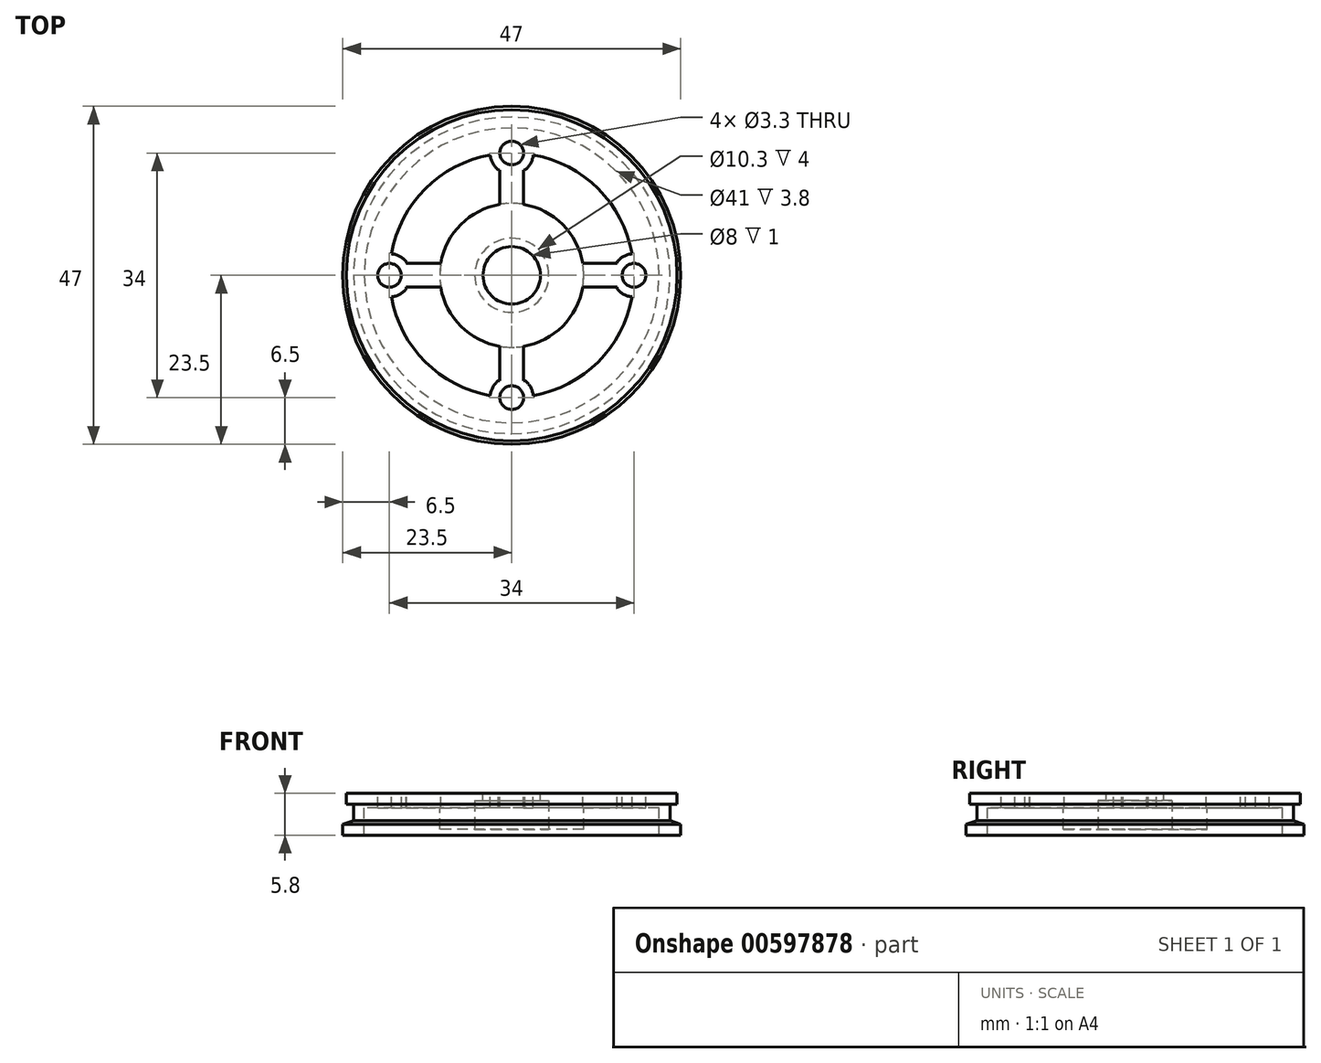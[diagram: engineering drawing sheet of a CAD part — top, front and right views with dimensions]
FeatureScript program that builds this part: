
annotation { "Feature Type Name" : "Feature", "Feature Type Description" : "" }
export const myFeature = defineFeature(function(context is Context, id is Id, definition is map)
    precondition{}
    {
        {
            var Q0;
            Q0=qCreatedBy(makeId("Front.planeOp"),FACE);
            var sketch = newSketch(context, id + "F0", { "sketchPlane" : qUnion([Q0])});
            skLineSegment(sketch, "E0", {"start": v(0, 18.35) * mm, "end": v(0, 16.35) * mm});
            skLineSegment(sketch, "E1", {"start": v(20.5, 12.55) * mm, "end": v(23, 12.55) * mm});
            skLineSegment(sketch, "E2", {"start": v(22, 16.85) * mm, "end": v(23, 16.85) * mm});
            skLineSegment(sketch, "E3", {"start": v(23, 16.85) * mm, "end": v(23, 18.35) * mm});
            skLineSegment(sketch, "E4", {"start": v(23, 18.35) * mm, "end": v(14.75, 18.35) * mm});
            skLineSegment(sketch, "E5", {"start": v(20.5, 12.55) * mm, "end": v(20.5, 16.35) * mm});
            skLineSegment(sketch, "E6", {"start": v(20.5, 16.35) * mm, "end": v(14.75, 16.35) * mm});
            skLineSegment(sketch, "E7", {"start": v(14.75, 18.35) * mm, "end": v(14.75, 16.35) * mm});
            skLineSegment(sketch, "E8", {"start": v(22, 16.85) * mm, "end": v(22, 14.58) * mm});
            skLineSegment(sketch, "E9.bottom", {"start": v(23, 14.05) * mm, "end": v(23.5, 14.05) * mm});
            skLineSegment(sketch, "E9.top", {"start": v(23, 12.55) * mm, "end": v(23.5, 12.55) * mm});
            skLineSegment(sketch, "E9.right", {"start": v(23.5, 14.05) * mm, "end": v(23.5, 12.55) * mm});
            skLineSegment(sketch, "E10", {"start": v(23.5, 14.05) * mm, "end": v(22, 14.58) * mm});
            skSolve(sketch);
        }
        {
            var Q0;
            Q0=makeQuery(id+"F0.imprint","IMPRINT",FACE,{"disambiguationData":[TD([[makeQuery(id+"F0.imprint","IMPRINT",EDGE,{"derivedFrom":sQuery(id+"F0.wireOp",EDGE,"E1")}),1.0]])]});
            var Q1;
            Q1=sQuery(id+"F0.wireOp",EDGE,"E0");
            revolve(context, id + "F1", {"entities" : qUnion([Q0]), "axis" : qUnion([Q1]), "revolveType" : RevolveType.FULL});
        }
        {
            var Q0;
            Q0=makeQuery(id+"F1.opRevolve","SWEPT_FACE",FACE,{"disambiguationData":[OSD([sQuery(id+"F0.wireOp",EDGE,"E4")])]});
            var sketch = newSketch(context, id + "F2", { "sketchPlane" : qUnion([Q0])});
            skCircle(sketch, "E11", {"center": v(0, 17) * mm, "radius": 1.65 * mm});
            skCircle(sketch, "E12", {"center": v(0, -17) * mm, "radius": 1.65 * mm});
            skCircle(sketch, "E13", {"center": v(17, 0) * mm, "radius": 1.65 * mm});
            skCircle(sketch, "E14", {"center": v(-17, 0) * mm, "radius": 1.65 * mm});
            skSolve(sketch);
        }
        {
            var Q0;
            Q0=makeQuery(id+"F2.imprint","IMPRINT",FACE,{"disambiguationData":[TD([[makeQuery(id+"F2.imprint","IMPRINT",EDGE,{"derivedFrom":sQuery(id+"F2.wireOp",EDGE,"E11")}),1.0]])]});
            var Q1;
            Q1=makeQuery(id+"F2.imprint","IMPRINT",FACE,{"disambiguationData":[TD([[makeQuery(id+"F2.imprint","IMPRINT",EDGE,{"derivedFrom":sQuery(id+"F2.wireOp",EDGE,"E13")}),1.0]])]});
            var Q2;
            Q2=makeQuery(id+"F2.imprint","IMPRINT",FACE,{"disambiguationData":[TD([[makeQuery(id+"F2.imprint","IMPRINT",EDGE,{"derivedFrom":sQuery(id+"F2.wireOp",EDGE,"E14")}),1.0]])]});
            var Q3;
            Q3=makeQuery(id+"F2.imprint","IMPRINT",FACE,{"disambiguationData":[TD([[makeQuery(id+"F2.imprint","IMPRINT",EDGE,{"derivedFrom":sQuery(id+"F2.wireOp",EDGE,"E12")}),1.0]])]});
            extrude(context, id + "F3", {"entities" : qUnion([Q0, Q1, Q2, Q3]), "operationType" : NewBodyOperationType.REMOVE, "endBound" : BoundingType.THROUGH_ALL, "oppositeDirection" : true, "depth" : 25 * mm, "offsetDistance" : 25 * mm});
        }
        {
            var Q0;
            Q0=makeQuery(id+"F1.opRevolve","SWEPT_FACE",FACE,{"disambiguationData":[OSD([sQuery(id+"F0.wireOp",EDGE,"E4")])]});
            var sketch = newSketch(context, id + "F4", { "sketchPlane" : qUnion([Q0])});
            skArc(sketch, "E15", {"start": v(-1.65, 9.86) * mm, "mid": v(-7.07, 7.07) * mm, "end": v(-9.86, 1.65) * mm});
            skLineSegment(sketch, "E16", {"start": v(-17.07, 1.65) * mm, "end": v(-9.86, 1.65) * mm});
            skLineSegment(sketch, "E17", {"start": v(17, -1.65) * mm, "end": v(9.86, -1.65) * mm});
            skLineSegment(sketch, "E18", {"start": v(1.65, 16.99) * mm, "end": v(1.65, 9.86) * mm});
            skLineSegment(sketch, "E19", {"start": v(-1.65, -17) * mm, "end": v(-1.65, -9.86) * mm});
            skLineSegment(sketch, "E20.trimOffspring", {"start": v(9.86, 1.65) * mm, "end": v(17, 1.65) * mm});
            skLineSegment(sketch, "E21.trimOffspring", {"start": v(-1.65, 9.86) * mm, "end": v(-1.65, 16.99) * mm});
            skLineSegment(sketch, "E22.trimOffspring", {"start": v(1.65, -9.86) * mm, "end": v(1.65, -17) * mm});
            skArc(sketch, "E23.trimOffspring", {"start": v(9.86, 1.65) * mm, "mid": v(7.07, 7.07) * mm, "end": v(1.65, 9.86) * mm});
            skLineSegment(sketch, "E24.trimOffspring", {"start": v(-9.86, -1.65) * mm, "end": v(-17, -1.65) * mm});
            skArc(sketch, "E25.trimOffspring", {"start": v(1.65, -9.86) * mm, "mid": v(7.07, -7.07) * mm, "end": v(9.86, -1.65) * mm});
            skArc(sketch, "E26.trimOffspring", {"start": v(-9.86, -1.65) * mm, "mid": v(-7.07, -7.07) * mm, "end": v(-1.65, -9.86) * mm});
            skSolve(sketch);
        }
        {
            var Q0;
            {var subQ5=sQuery(id+"F4.wireOp",EDGE,"E15");Q0=makeQuery(id+"F4.imprint","IMPRINT",FACE,{"disambiguationData":[TD([[makeQuery(id+"F4.imprint","IMPRINT",EDGE,{"derivedFrom":subQ5}),1.0]])]});}
            var Q1;
            {var subQ0=sQuery(id+"F4.wireOp",EDGE,"E18");var subQ1=makeQuery(id+"F3.boolean.opBoolean","COPY",EDGE,{"derivedFrom":makeQuery(id+"F3.opExtrude","CAP_EDGE",EDGE,{"disambiguationData":[OSD([sQuery(id+"F2.wireOp",EDGE,"E11")])],"isStart":true})});var subQ2=makeQuery(id+"F4.imprint","INTERSECT",VERTEX,{"derivedFrom":[subQ1,subQ0]});Q1=makeQuery(id+"F4.imprint","IMPRINT",FACE,{"disambiguationData":[TD([[makeQuery(id+"F4.imprint","IMPRINT",EDGE,{"disambiguationData":[TD([[subQ2,1.0]])],"derivedFrom":subQ1}),-1.0]])]});}
            var Q2;
            {var subQ0=sQuery(id+"F4.wireOp",EDGE,"E17");var subQ1=makeQuery(id+"F3.boolean.opBoolean","COPY",EDGE,{"derivedFrom":makeQuery(id+"F3.opExtrude","CAP_EDGE",EDGE,{"disambiguationData":[OSD([sQuery(id+"F2.wireOp",EDGE,"E13")])],"isStart":true})});var subQ2=makeQuery(id+"F4.imprint","INTERSECT",VERTEX,{"derivedFrom":[subQ1,subQ0]});Q2=makeQuery(id+"F4.imprint","IMPRINT",FACE,{"disambiguationData":[TD([[makeQuery(id+"F4.imprint","IMPRINT",EDGE,{"disambiguationData":[TD([[subQ2,1.0]])],"derivedFrom":subQ1}),-1.0]])]});}
            var Q3;
            {var subQ1=makeQuery(id+"F3.boolean.opBoolean","COPY",EDGE,{"derivedFrom":makeQuery(id+"F3.opExtrude","CAP_EDGE",EDGE,{"disambiguationData":[OSD([sQuery(id+"F2.wireOp",EDGE,"E14")])],"isStart":true})});var subQ5=sQuery(id+"F4.wireOp",EDGE,"E24.trimOffspring");var subQ6=makeQuery(id+"F4.imprint","INTERSECT",VERTEX,{"derivedFrom":[subQ1,subQ5]});Q3=makeQuery(id+"F4.imprint","IMPRINT",FACE,{"disambiguationData":[TD([[makeQuery(id+"F4.imprint","IMPRINT",EDGE,{"disambiguationData":[TD([[subQ6,-1.0]])],"derivedFrom":subQ1}),-1.0]])]});}
            var Q4;
            {var subQ0=sQuery(id+"F4.wireOp",EDGE,"E19");var subQ1=makeQuery(id+"F3.boolean.opBoolean","COPY",EDGE,{"derivedFrom":makeQuery(id+"F3.opExtrude","CAP_EDGE",EDGE,{"disambiguationData":[OSD([sQuery(id+"F2.wireOp",EDGE,"E12")])],"isStart":true})});var subQ2=makeQuery(id+"F4.imprint","INTERSECT",VERTEX,{"derivedFrom":[subQ1,subQ0]});Q4=makeQuery(id+"F4.imprint","IMPRINT",FACE,{"disambiguationData":[TD([[makeQuery(id+"F4.imprint","IMPRINT",EDGE,{"disambiguationData":[TD([[subQ2,1.0]])],"derivedFrom":subQ1}),-1.0]])]});}
            extrude(context, id + "F5", {"entities" : qUnion([Q0, Q1, Q2, Q3, Q4]), "operationType" : NewBodyOperationType.ADD, "oppositeDirection" : true, "depth" : 2 * mm, "offsetDistance" : 25 * mm});
        }
        {
            var Q0;
            Q0=makeQuery(id+"F5.boolean.opBoolean","MERGE",FACE,{"derivedFrom":[makeQuery(id+"F1.opRevolve","SWEPT_FACE",FACE,{"disambiguationData":[OSD([sQuery(id+"F0.wireOp",EDGE,"E4")])]}),makeQuery(id+"F5.opExtrude","CAP_FACE",FACE,{"disambiguationData":[OSD([sQuery(id+"F2.wireOp",EDGE,"E11"),sQuery(id+"F2.wireOp",EDGE,"E12"),sQuery(id+"F2.wireOp",EDGE,"E13"),sQuery(id+"F2.wireOp",EDGE,"E14"),sQuery(id+"F4.wireOp",EDGE,"E15"),sQuery(id+"F4.wireOp",EDGE,"E16"),sQuery(id+"F4.wireOp",EDGE,"E17"),sQuery(id+"F4.wireOp",EDGE,"E18"),sQuery(id+"F4.wireOp",EDGE,"E19"),sQuery(id+"F4.wireOp",EDGE,"E20.trimOffspring"),sQuery(id+"F4.wireOp",EDGE,"E21.trimOffspring"),sQuery(id+"F4.wireOp",EDGE,"E22.trimOffspring"),sQuery(id+"F4.wireOp",EDGE,"E23.trimOffspring"),sQuery(id+"F4.wireOp",EDGE,"E24.trimOffspring"),sQuery(id+"F4.wireOp",EDGE,"E25.trimOffspring"),sQuery(id+"F4.wireOp",EDGE,"E26.trimOffspring")])],"isStart":true})]});
            var sketch = newSketch(context, id + "F6", { "sketchPlane" : qUnion([Q0])});
            skArc(sketch, "E27", {"start": v(-2.99, 16.74) * mm, "mid": v(-12.02, 12.02) * mm, "end": v(-16.74, 2.99) * mm});
            skArc(sketch, "E28", {"start": v(-2.99, 16.74) * mm, "mid": v(0, 14) * mm, "end": v(2.99, 16.74) * mm});
            skArc(sketch, "E29", {"start": v(16.74, 2.99) * mm, "mid": v(14, 0) * mm, "end": v(16.74, -2.99) * mm});
            skArc(sketch, "E30", {"start": v(-16.74, -2.99) * mm, "mid": v(-14, 0) * mm, "end": v(-16.74, 2.99) * mm});
            skArc(sketch, "E31", {"start": v(2.99, -16.74) * mm, "mid": v(0, -14) * mm, "end": v(-2.99, -16.74) * mm});
            skPoint(sketch, "E32.0.midPoint", {"position": v(3.11, -5.36) * mm});
            skArc(sketch, "E33.trimOffspring", {"start": v(-16.74, -2.99) * mm, "mid": v(-12.02, -12.02) * mm, "end": v(-2.99, -16.74) * mm});
            skArc(sketch, "E34.trimOffspring", {"start": v(2.99, -16.74) * mm, "mid": v(12.02, -12.02) * mm, "end": v(16.74, -2.99) * mm});
            skArc(sketch, "E35.trimOffspring", {"start": v(16.74, 2.99) * mm, "mid": v(12.02, 12.02) * mm, "end": v(2.99, 16.74) * mm});
            skPoint(sketch, "E36.orphan", {"position": v(-0.02, 7.16) * mm});
            skPoint(sketch, "E37.orphan", {"position": v(0.02, -7.16) * mm});
            skPoint(sketch, "E38.orphan", {"position": v(6.2, -3.56) * mm});
            skSolve(sketch);
        }
        {
            var Q0;
            {var subQ0=sQuery(id+"F6.wireOp",EDGE,"E27");Q0=makeQuery(id+"F6.imprint","IMPRINT",FACE,{"disambiguationData":[TD([[makeQuery(id+"F6.imprint","IMPRINT",EDGE,{"derivedFrom":subQ0}),1.0]])]});}
            var Q1;
            {var subQ0=sQuery(id+"F6.wireOp",EDGE,"E35.trimOffspring");Q1=makeQuery(id+"F6.imprint","IMPRINT",FACE,{"disambiguationData":[TD([[makeQuery(id+"F6.imprint","IMPRINT",EDGE,{"derivedFrom":subQ0}),1.0]])]});}
            var Q2;
            {var subQ0=sQuery(id+"F6.wireOp",EDGE,"E34.trimOffspring");Q2=makeQuery(id+"F6.imprint","IMPRINT",FACE,{"disambiguationData":[TD([[makeQuery(id+"F6.imprint","IMPRINT",EDGE,{"derivedFrom":subQ0}),1.0]])]});}
            var Q3;
            {var subQ0=sQuery(id+"F6.wireOp",EDGE,"E33.trimOffspring");Q3=makeQuery(id+"F6.imprint","IMPRINT",FACE,{"disambiguationData":[TD([[makeQuery(id+"F6.imprint","IMPRINT",EDGE,{"derivedFrom":subQ0}),1.0]])]});}
            var Q4;
            Q4=makeQuery(id+"F6.imprint","IMPRINT",FACE,{"disambiguationData":[TD([[makeQuery(id+"F6.imprint","IMPRINT",EDGE,{"derivedFrom":sQuery(id+"F6.wireOp",EDGE,"E32.0")}),-1.0]])]});
            extrude(context, id + "F7", {"entities" : qUnion([Q0, Q1, Q2, Q3, Q4]), "operationType" : NewBodyOperationType.REMOVE, "endBound" : BoundingType.THROUGH_ALL, "oppositeDirection" : true, "depth" : 25 * mm, "offsetDistance" : 25 * mm});
        }
        {
            var Q0;
            Q0=makeQuery(id+"F5.boolean.opBoolean","MERGE",FACE,{"derivedFrom":[makeQuery(id+"F1.opRevolve","SWEPT_FACE",FACE,{"disambiguationData":[OSD([sQuery(id+"F0.wireOp",EDGE,"E6")])]}),makeQuery(id+"F5.opExtrude","CAP_FACE",FACE,{"disambiguationData":[OSD([sQuery(id+"F2.wireOp",EDGE,"E11"),sQuery(id+"F2.wireOp",EDGE,"E12"),sQuery(id+"F2.wireOp",EDGE,"E13"),sQuery(id+"F2.wireOp",EDGE,"E14"),sQuery(id+"F4.wireOp",EDGE,"E15"),sQuery(id+"F4.wireOp",EDGE,"E16"),sQuery(id+"F4.wireOp",EDGE,"E17"),sQuery(id+"F4.wireOp",EDGE,"E18"),sQuery(id+"F4.wireOp",EDGE,"E19"),sQuery(id+"F4.wireOp",EDGE,"E20.trimOffspring"),sQuery(id+"F4.wireOp",EDGE,"E21.trimOffspring"),sQuery(id+"F4.wireOp",EDGE,"E22.trimOffspring"),sQuery(id+"F4.wireOp",EDGE,"E23.trimOffspring"),sQuery(id+"F4.wireOp",EDGE,"E24.trimOffspring"),sQuery(id+"F4.wireOp",EDGE,"E25.trimOffspring"),sQuery(id+"F4.wireOp",EDGE,"E26.trimOffspring")])],"isStart":false})]});
            var sketch = newSketch(context, id + "F8", { "sketchPlane" : qUnion([Q0])});
            skCircle(sketch, "E39", {"center": v(0, 0) * mm, "radius": 10 * mm});
            skSolve(sketch);
        }
        {
            var Q0;
            {var subQ3=sQuery(id+"F4.wireOp",EDGE,"E20.trimOffspring");var subQ5=sQuery(id+"F4.wireOp",EDGE,"E18");var subQ9=sQuery(id+"F8.wireOp",EDGE,"E39");var subQ11=makeQuery(id+"F8.imprint","INTERSECT",VERTEX,{"derivedFrom":[makeQuery(id+"F5.opExtrude","CAP_EDGE",EDGE,{"disambiguationData":[OSD([subQ3])],"isStart":false}),subQ9]});var subQ13=makeQuery(id+"F8.imprint","INTERSECT",VERTEX,{"derivedFrom":[makeQuery(id+"F5.opExtrude","CAP_EDGE",EDGE,{"disambiguationData":[OSD([subQ5])],"isStart":false}),subQ9]});Q0=makeQuery(id+"F8.imprint","IMPRINT",FACE,{"disambiguationData":[TD([[makeQuery(id+"F8.imprint","IMPRINT",EDGE,{"disambiguationData":[TD([[subQ13,1.0],[subQ11,-1.0]])],"derivedFrom":subQ9}),-1.0]])]});}
            extrude(context, id + "F9", {"entities" : qUnion([Q0]), "operationType" : NewBodyOperationType.ADD, "depth" : 5 * mm, "offsetDistance" : 25 * mm});
        }
        {
            var Q0;
            Q0=makeQuery(id+"F5.boolean.opBoolean","MERGE",FACE,{"derivedFrom":[makeQuery(id+"F1.opRevolve","SWEPT_FACE",FACE,{"disambiguationData":[OSD([sQuery(id+"F0.wireOp",EDGE,"E4")])]}),makeQuery(id+"F5.opExtrude","CAP_FACE",FACE,{"disambiguationData":[OSD([sQuery(id+"F2.wireOp",EDGE,"E11"),sQuery(id+"F2.wireOp",EDGE,"E12"),sQuery(id+"F2.wireOp",EDGE,"E13"),sQuery(id+"F2.wireOp",EDGE,"E14"),sQuery(id+"F4.wireOp",EDGE,"E15"),sQuery(id+"F4.wireOp",EDGE,"E16"),sQuery(id+"F4.wireOp",EDGE,"E17"),sQuery(id+"F4.wireOp",EDGE,"E18"),sQuery(id+"F4.wireOp",EDGE,"E19"),sQuery(id+"F4.wireOp",EDGE,"E20.trimOffspring"),sQuery(id+"F4.wireOp",EDGE,"E21.trimOffspring"),sQuery(id+"F4.wireOp",EDGE,"E22.trimOffspring"),sQuery(id+"F4.wireOp",EDGE,"E23.trimOffspring"),sQuery(id+"F4.wireOp",EDGE,"E24.trimOffspring"),sQuery(id+"F4.wireOp",EDGE,"E25.trimOffspring"),sQuery(id+"F4.wireOp",EDGE,"E26.trimOffspring")])],"isStart":true})]});
            var sketch = newSketch(context, id + "F10", { "sketchPlane" : qUnion([Q0])});
            skCircle(sketch, "E40", {"center": v(0, 0) * mm, "radius": 4 * mm});
            skSolve(sketch);
        }
        {
            var Q0;
            Q0=makeQuery(id+"F9.opExtrude","CAP_FACE",FACE,{"disambiguationData":[OSD([sQuery(id+"F8.wireOp",EDGE,"E39")])],"isStart":false});
            var sketch = newSketch(context, id + "F11", { "sketchPlane" : qUnion([Q0])});
            skCircle(sketch, "E41", {"center": v(0, 0) * mm, "radius": 5.15 * mm});
            skSolve(sketch);
        }
        {
            var Q0;
            Q0=makeQuery(id+"F11.imprint","IMPRINT",FACE,{"disambiguationData":[TD([[makeQuery(id+"F11.imprint","IMPRINT",EDGE,{"derivedFrom":sQuery(id+"F11.wireOp",EDGE,"E41")}),1.0]])]});
            extrude(context, id + "F12", {"entities" : qUnion([Q0]), "operationType" : NewBodyOperationType.REMOVE, "oppositeDirection" : true, "depth" : 6 * mm, "offsetDistance" : 25 * mm});
        }
        {
            var Q0;
            Q0=makeQuery(id+"F10.imprint","IMPRINT",FACE,{"disambiguationData":[TD([[makeQuery(id+"F10.imprint","IMPRINT",EDGE,{"derivedFrom":sQuery(id+"F10.wireOp",EDGE,"E40")}),1.0]])]});
            extrude(context, id + "F13", {"entities" : qUnion([Q0]), "operationType" : NewBodyOperationType.REMOVE, "endBound" : BoundingType.THROUGH_ALL, "oppositeDirection" : true, "depth" : 25 * mm, "offsetDistance" : 25 * mm});
        }
        {
            var Q0;
            Q0=makeQuery(id+"F9.opExtrude","CAP_FACE",FACE,{"disambiguationData":[OSD([sQuery(id+"F8.wireOp",EDGE,"E39")])],"isStart":false});
            extrude(context, id + "F14", {"entities" : qUnion([Q0]), "operationType" : NewBodyOperationType.REMOVE, "oppositeDirection" : true, "depth" : 2 * mm, "offsetDistance" : 25 * mm});
        }
    });
